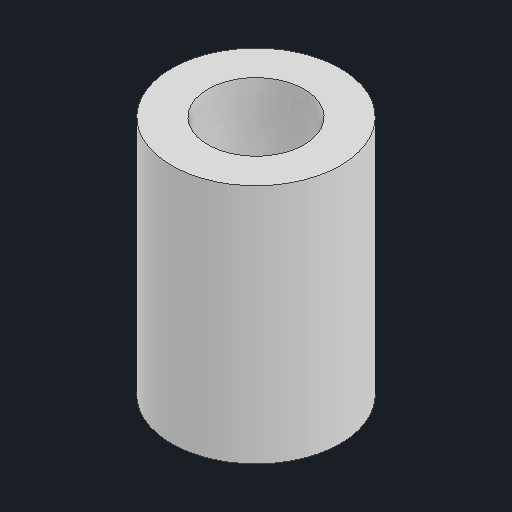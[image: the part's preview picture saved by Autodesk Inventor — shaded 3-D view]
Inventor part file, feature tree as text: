
AUTODESK INVENTOR PART (.ipt)
format: ipt  version: 2024 (Build 280153000, 153)  size: 168,448 bytes
history: native  units: in
note: dims shown in document units (in); Inventor stores cm internally (conversion verified against a paired STEP export)
features: extrude x1, sketch x1
ambient origin geometry x8: Origin, YZ Plane, XZ Plane, XY Plane, X Axis, Y Axis, Z Axis, Center Point
bodies: Solid1 (feature_tree)
feature tree (2):
  extrude  "Extrusion1"  Depth=0.3937in
  sketch  "Sketch1"  dims[d0=0.1575in d1=0.2756in d2=0.3937in d3=0.0in]
